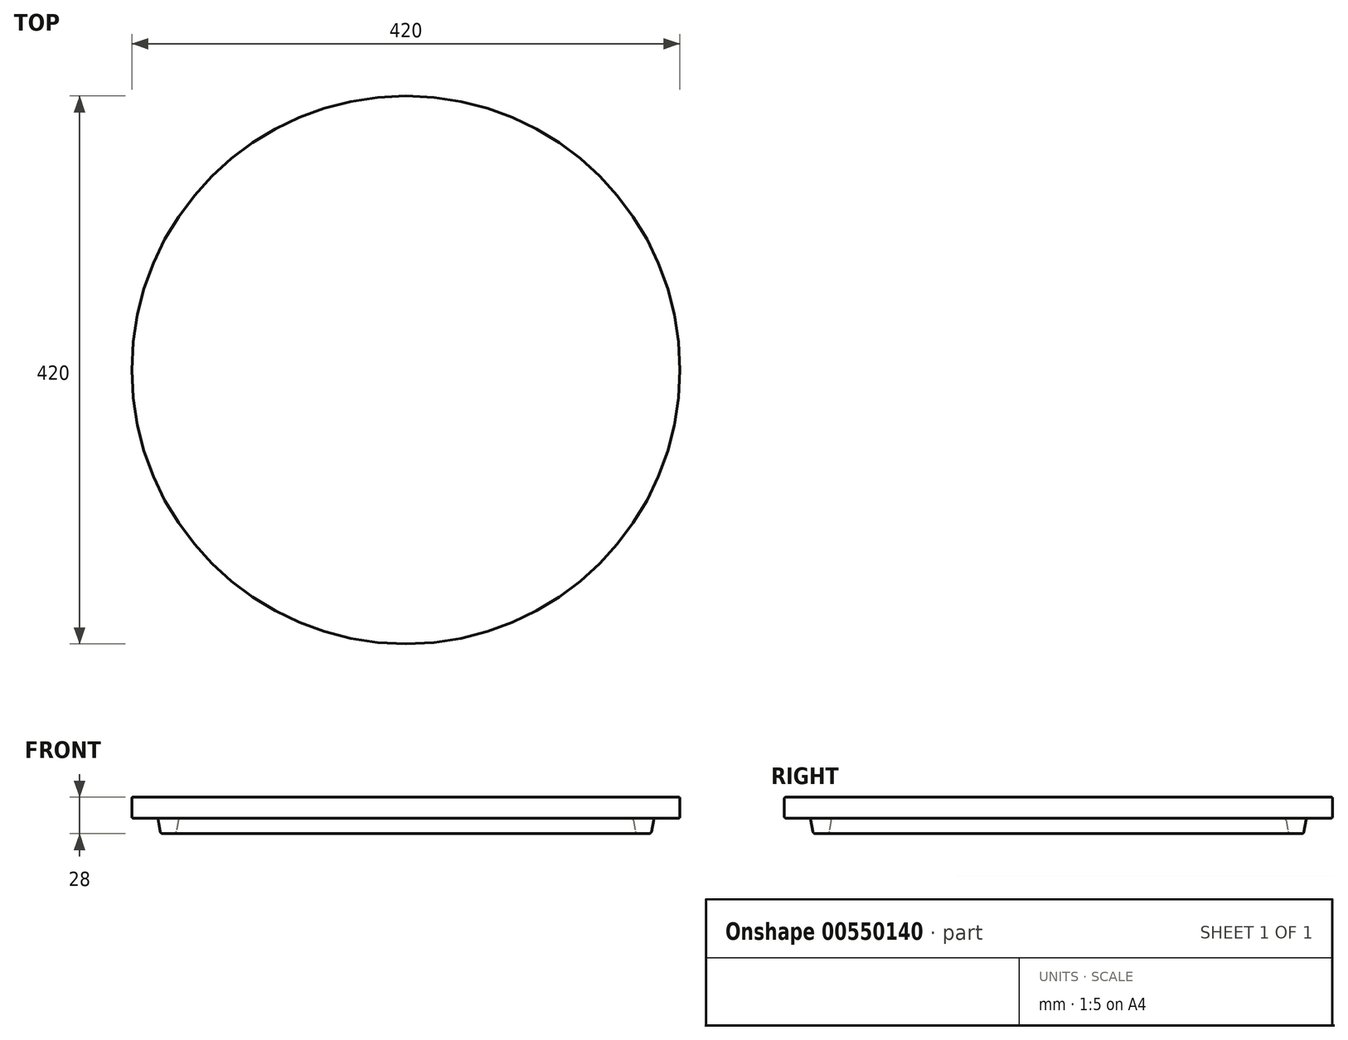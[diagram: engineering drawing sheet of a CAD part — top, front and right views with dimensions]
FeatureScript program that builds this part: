
annotation { "Feature Type Name" : "Feature", "Feature Type Description" : "" }
export const myFeature = defineFeature(function(context is Context, id is Id, definition is map)
    precondition{}
    {
        {
            var Q0;
            Q0=qCreatedBy(makeId("Front.planeOp"),FACE);
            var sketch = newSketch(context, id + "F0", { "sketchPlane" : qUnion([Q0])});
            skLineSegment(sketch, "E0", {"start": v(0, 0) * mm, "end": v(210, 0) * mm, "construction": true});
            skLineSegment(sketch, "E1", {"start": v(209, 28) * mm, "end": v(0, 28) * mm});
            skLineSegment(sketch, "E2", {"start": v(0, 28) * mm, "end": v(0, 12) * mm});
            skLineSegment(sketch, "E3", {"start": v(0, 12) * mm, "end": v(172.32, 12) * mm});
            skLineSegment(sketch, "E4", {"start": v(174.3, 10.35) * mm, "end": v(175.82, 1.65) * mm});
            skLineSegment(sketch, "E5", {"start": v(177.8, 0) * mm, "end": v(186.2, 0) * mm});
            skLineSegment(sketch, "E6", {"start": v(188.18, 1.65) * mm, "end": v(189.7, 10.35) * mm});
            skPoint(sketch, "E7.visualSharp", {"position": v(190, 12) * mm});
            skArc(sketch, "E7.filletArc", {"start": v(191.68, 12) * mm, "mid": v(190.4, 11.53) * mm, "end": v(189.7, 10.35) * mm});
            skPoint(sketch, "E8.visualSharp", {"position": v(174, 12) * mm});
            skArc(sketch, "E8.filletArc", {"start": v(174.3, 10.35) * mm, "mid": v(173.6, 11.53) * mm, "end": v(172.32, 12) * mm});
            skPoint(sketch, "E9.visualSharp", {"position": v(187.88, 0) * mm});
            skArc(sketch, "E9.filletArc", {"start": v(186.2, 0) * mm, "mid": v(187.5, 0.47) * mm, "end": v(188.18, 1.65) * mm});
            skPoint(sketch, "E10.visualSharp", {"position": v(176.12, 0) * mm});
            skArc(sketch, "E10.filletArc", {"start": v(175.82, 1.65) * mm, "mid": v(176.5, 0.47) * mm, "end": v(177.8, 0) * mm});
            skLineSegment(sketch, "E11", {"start": v(0, 0) * mm, "end": v(0, 28) * mm, "construction": true});
            skArc(sketch, "E12.filletArc", {"start": v(210, 27) * mm, "mid": v(209.7, 27.7) * mm, "end": v(209, 28) * mm});
            skLineSegment(sketch, "E13", {"start": v(191.68, 12) * mm, "end": v(209, 12) * mm});
            skLineSegment(sketch, "E14", {"start": v(210, 13) * mm, "end": v(210, 27) * mm});
            skArc(sketch, "E15.filletArc", {"start": v(209, 12) * mm, "mid": v(209.7, 12.3) * mm, "end": v(210, 13) * mm});
            skSolve(sketch);
        }
        {
            var Q0;
            Q0=makeQuery(id+"F0.imprint","IMPRINT",FACE,{"disambiguationData":[TD([[makeQuery(id+"F0.imprint","IMPRINT",EDGE,{"derivedFrom":sQuery(id+"F0.wireOp",EDGE,"E1")}),1.0]])]});
            var Q1;
            Q1=sQuery(id+"F0.wireOp",EDGE,"E11");
            revolve(context, id + "F1", {"entities" : qUnion([Q0]), "axis" : qUnion([Q1]), "revolveType" : RevolveType.FULL});
        }
    });
